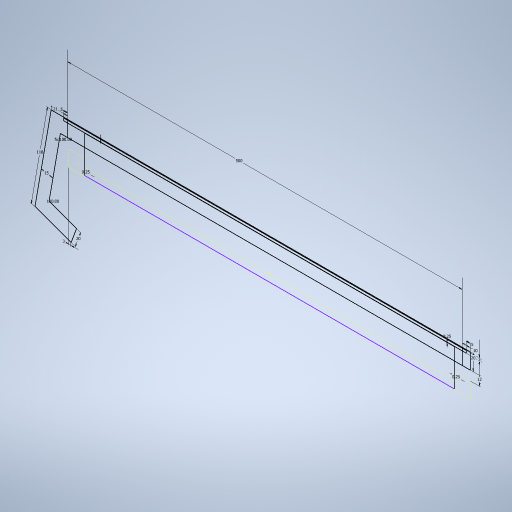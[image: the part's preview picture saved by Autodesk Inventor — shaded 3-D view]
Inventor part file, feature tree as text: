
AUTODESK INVENTOR PART (.ipt)
format: ipt  version: 2024 (Build 280153000, 153)  size: 310,784 bytes
history: native  units: mm
features: sketch x4
ambient origin geometry x8: Origin, YZ Plane, XZ Plane, XY Plane, X Axis, Y Axis, Z Axis, Center Point
feature tree (4):
  sketch  "Sketch1"  dims[d0=488.7mm]
  sketch  "Sketch2"  dims[d1=20.0mm]
  sketch  "Sketch3"  dims[d2=20.0mm]
  sketch  "Sketch4"  dims[d3=20.0mm d4=20.0mm d5=20.0mm d6=12.0mm d7=17.453293mm d8=17.453293mm d9=20.0mm d10=15.0mm d11=1.0mm d13=3.0mm d14=3.25mm d15=10.0mm d16=3.0mm d17=2.0mm d18=7.0mm d19=16.0mm d20=4.25mm d21=10.0mm d22=1.0mm d23=3.0mm d24=118.0mm d27=16.0mm d28=5.0mm d29=500.0mm d30=20.0mm d31=12.0mm d32=15.0mm d33=20.0mm d34=17.453293mm d35=17.453293mm d36=118.0mm d37=21.0mm d38=10.0mm d39=500.0mm d40=3.0mm d41=3.0mm d42=1.0mm d43=5.0mm d44=5.0mm d45=0.25mm d46=0.25mm d47=0.25mm]
